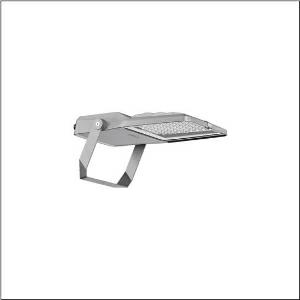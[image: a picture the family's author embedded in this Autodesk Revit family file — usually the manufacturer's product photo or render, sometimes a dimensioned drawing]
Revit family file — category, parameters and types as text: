
# Revit family: floodlight_fl_21_iq_mini___pl52_5xa7772d5d1a_a443
name_source: partatom
category: Lighting Fixtures
units: mm (PartAtom-declared; Revit-internal decimal feet)

## family parameters
Cut with Voids When Loaded = No
Host = Face
Light Source = No
Part Type = Normal
Room Calculation Point = No
Round Connector Dimension = Use Diameter
Shared = No

## types (1)
- --- (1 x LED, 16640 lm, 143 W, 4000K)
    Apparent Load = 143 VA
    CIE Flux Codes = 26 60 98 100 100
    Color Rendering = 80
    Color Temperature = 4000K
    Default Elevation = 1800 mm
    Description = Floodlight FL 21 iQ mini, floodlight, primary light control with lens, of PMMA, primary optical cover: protective disc, of toughened safety glass, transparent, light distribution: PL52, light emission: direct distribution, installation type: surface-mounted, LED, High Power LED, rated luminous flux: 16.640lm, luminous efficacy: 116lm/W, light colour: 840, colour temperature: 4000K, control gear: iQ Street-Remote/DALI, control: Street-Remote, Auto-Match, Temp-Guard, Night-Set, Smart-Wire, Desk-Remote (wireless, voltage-free reading and setting of iQ features in the workshop via application-optimized NFC function/RFID function), optimised constant luminous flux control (CLO 2.0), with terminal, 6-pole, mains connection: 220..240V, AC, 50/60Hz, start of lifetime: 143W, end of service life: 152W, reduction: 61W, luminaire housing, of diecast aluminium, powder-coated, Siteco® metallic grey (DB 702S), corrosivity category C5 mid according to DIN EN ISO 12944, suitable for swimming pools, chlorine-resistant, sealing non-destructively replaceable, mounting bracket, of steel, galvanised, powder-coated, Siteco® metallic grey (DB 702S), protection rating (complete): IP66, insulation class (complete): insulation class II (safety insulation), certification: CE, ENEC, VDE, protection symbol: D, impact resistance: IK08, permissible operating ambient temperature: -40..+40°C, permissible operating ambient temperature for outdoor applications: -40..+50°C, standard: DIN EN 12944, LABS conformity tested according to VDMA 24364:2018-05, packaging unit: 1 piece

Light Distribution: PL52
    Height = 70 mm
    Lamp = 1 x LED
    Lamp Light Flux = 16640 lm
    Lamp Power = 143 W
    Lamp count = 1
    Length = 485 mm
    Luminous efficacy = 116 lm/W
    Manufacturer = Siteco
    ModVariant = No
    Model = 5XA7772D5D1A
    Number of Poles = 1
    OnlyDefault = Yes
    Power Factor = 1
    Product Name = Floodlight FL 21 iQ mini | PL52
    Product group = floodlight | pylon annexe
    ProductGroupID = 6200
    Protection Class = Protection class II
    Protection Degree = IP 66
    RLX_Detail_Level = 1
    RLX_Emergency_Light_Flux = 0 lm
    RLX_Emergency_Type = 0
    RLX_Emergency_Type_DB = No
    RlxData = <blob elided: 96805 chars, md5=c63e9e17>
    Socket = socket
    Standby Power = 0 W
    System Light Flux = 16640 lm
    System Power = 143 W
    Type Comments = factory setting: luminous flux: 100 % | dim-lin: 254 | 730 mA
    Type Image = l_1006845.jpg
    URL = http://relux.com
    VarID = @adj_163522
    Voltage = 0 V
    Weight = 0.00 kg
    Width = 337 mm

## geometry (parser evidence)
native form markers: Blend x4, Sweep x13
no freeform markers — native parametric forms only
